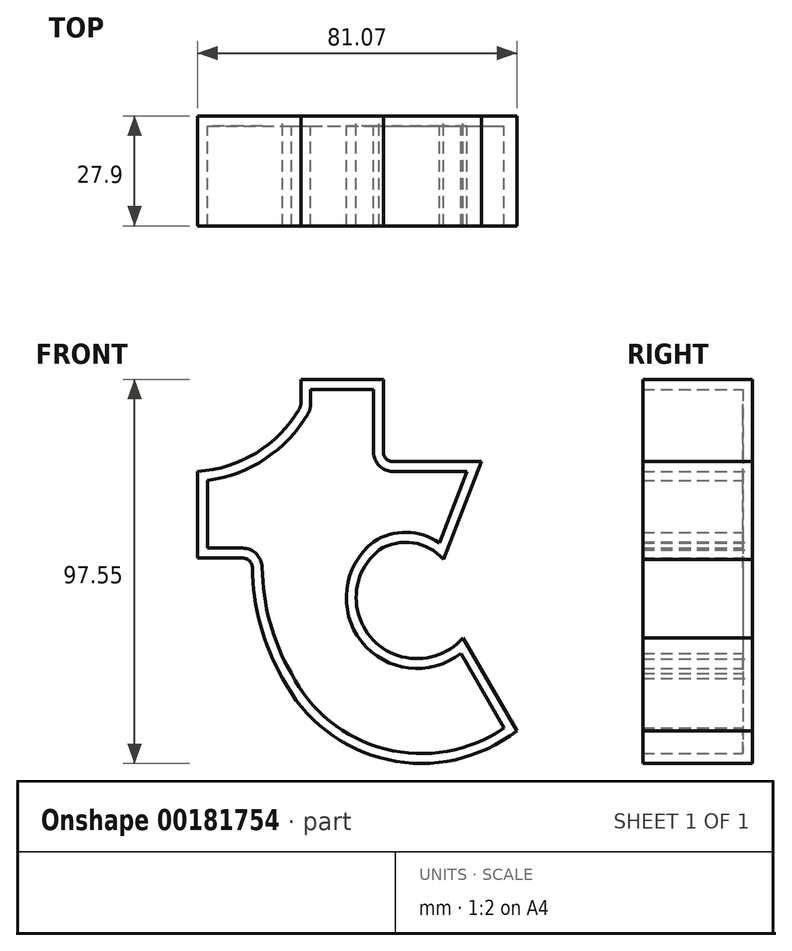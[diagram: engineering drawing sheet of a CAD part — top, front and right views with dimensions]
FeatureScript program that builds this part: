
annotation { "Feature Type Name" : "Feature", "Feature Type Description" : "" }
export const myFeature = defineFeature(function(context is Context, id is Id, definition is map)
    precondition{}
    {
        {
            var Q0;
            Q0=qCreatedBy(makeId("Front.planeOp"),FACE);
            var sketch = newSketch(context, id + "F0", { "sketchPlane" : qUnion([Q0])});
            skText(sketch, "E0", { "text": "t", "fontName": "RobotoSlab-Bold.ttf"});
            const initialGuessF0  = {"E0": [-0.0626, -0.05378, 1, 0, 0.109]};
            skSetInitialGuess(sketch, initialGuessF0);
            skSolve(sketch);
        }
        {
            var Q0;
            Q0=makeQuery(id+"F0.imprint","IMPRINT",FACE,{"disambiguationData":[TD([[makeQuery(id+"F0.imprint","IMPRINT",EDGE,{"derivedFrom":sQuery(id+"F0.wireOp",EDGE,"E0.sketch_text.stroke-0")}),-1.0]])]});
            var sketch = newSketch(context, id + "F1", { "sketchPlane" : qUnion([Q0])});
            skLineSegment(sketch, "E1", {"start": v(-44.06, 46.21) * mm, "end": v(-27.3, 46.21) * mm});
            skLineSegment(sketch, "E2", {"start": v(-27.3, 46.21) * mm, "end": v(-27.3, 29.9) * mm});
            skLineSegment(sketch, "E3", {"start": v(-27.3, 29.9) * mm, "end": v(-3.48, 29.9) * mm});
            skLineSegment(sketch, "E4", {"start": v(-5.08, -16.34) * mm, "end": v(5.84, -35.3) * mm});
            skLineSegment(sketch, "E5", {"start": v(-55.4, 10.4) * mm, "end": v(-69.45, 10.4) * mm});
            skLineSegment(sketch, "E6", {"start": v(-69.45, 10.4) * mm, "end": v(-69.45, 27.63) * mm});
            skArc(sketch, "E7", {"start": v(-27.3, 12) * mm, "mid": v(-30.36, -13.27) * mm, "end": v(-5.08, -16.34) * mm});
            skArc(sketch, "E8", {"start": v(-48.16, -21.43) * mm, "mid": v(-24.3, -40.6) * mm, "end": v(5.84, -35.3) * mm});
            skLineSegment(sketch, "E9", {"start": v(-3.48, 29.9) * mm, "end": v(-10.52, 11.76) * mm});
            skArc(sketch, "E10", {"start": v(-55.4, 10.4) * mm, "mid": v(-54.17, -6.06) * mm, "end": v(-48.16, -21.43) * mm});
            skArc(sketch, "E11", {"start": v(-10.52, 11.76) * mm, "mid": v(-18.87, 14.42) * mm, "end": v(-27.3, 12) * mm});
            skArc(sketch, "E12", {"start": v(-69.45, 27.63) * mm, "mid": v(-53.96, 33.68) * mm, "end": v(-43.02, 46.21) * mm});
            skSolve(sketch);
        }
        {
            var Q0;
            Q0=makeQuery(id+"F1.imprint","IMPRINT",FACE,{"disambiguationData":[TD([[makeQuery(id+"F1.imprint","IMPRINT",EDGE,{"derivedFrom":sQuery(id+"F1.wireOp",EDGE,"E5")}),-1.0]])]});
            var Q1;
            {var subQ24=makeQuery(id+"F0.imprint","IMPRINT",EDGE,{"derivedFrom":sQuery(id+"F0.wireOp",EDGE,"E0.sketch_text.stroke-1")});Q1=makeQuery(id+"F1.imprint","IMPRINT",FACE,{"disambiguationData":[TD([[makeQuery(id+"F1.imprint","IMPRINT",EDGE,{"derivedFrom":subQ24}),-1.0]])]});}
            var Q2;
            {var subQ1=sQuery(id+"F1.wireOp",EDGE,"E9");Q2=makeQuery(id+"F1.imprint","IMPRINT",FACE,{"disambiguationData":[TD([[makeQuery(id+"F1.imprint","IMPRINT",EDGE,{"derivedFrom":subQ1}),-1.0]])]});}
            var Q3;
            {var subQ1=sQuery(id+"F1.wireOp",EDGE,"E4");Q3=makeQuery(id+"F1.imprint","IMPRINT",FACE,{"disambiguationData":[TD([[makeQuery(id+"F1.imprint","IMPRINT",EDGE,{"derivedFrom":subQ1}),-1.0]])]});}
            extrude(context, id + "F2", {"entities" : qUnion([Q0, Q1, Q2, Q3]), "depth" : 25.4 * mm});
        }
        {
            var Q0;
            Q0=makeQuery(id+"F2.opExtrude","SWEPT_FACE",FACE,{"disambiguationData":[OSD([sQuery(id+"F0.wireOp",EDGE,"E0.sketch_text.stroke-19")])]});
            extrude(context, id + "F3", {"entities" : qUnion([Q0]), "operationType" : NewBodyOperationType.ADD, "depth" : 5 * mm});
        }
        {
            var Q0;
            Q0=makeQuery(id+"F2.opExtrude","SWEPT_EDGE",EDGE,{"disambiguationData":[OSD([sQuery(id+"F1.wireOp",EDGE,"E2"),sQuery(id+"F1.wireOp",EDGE,"E3")])]});
            var Q1;
            {var subQ0=sQuery(id+"F1.wireOp",EDGE,"E12");var subQ1=sQuery(id+"F0.wireOp",EDGE,"E0.sketch_text.stroke-19");Q1=makeQuery(id+"F3.boolean.opBoolean","MERGE",EDGE,{"derivedFrom":[makeQuery(id+"F2.opExtrude","SWEPT_EDGE",EDGE,{"disambiguationData":[OSD([subQ1,subQ0])]}),makeQuery(id+"F3.opExtrude","CAP_EDGE",EDGE,{"disambiguationData":[OSD([subQ1,subQ0])],"isStart":true})]});}
            var Q2;
            Q2=makeQuery(id+"F2.opExtrude","SWEPT_EDGE",EDGE,{"disambiguationData":[OSD([sQuery(id+"F1.wireOp",EDGE,"E5"),sQuery(id+"F1.wireOp",EDGE,"E10")])]});
            fillet(context, id + "F4", {"entities" : qUnion([Q0, Q1, Q2]), "radius" : 5 * mm, "tangentPropagation" : true, "allowEdgeOverflow" : false});
        }
        {
            var Q0;
            {var subQ0=sQuery(id+"F0.wireOp",EDGE,"E0.sketch_text.stroke-19");Q0=makeQuery(id+"F3.boolean.opBoolean","MERGE",FACE,{"derivedFrom":[makeQuery(id+"F2.opExtrude","CAP_FACE",FACE,{"disambiguationData":[OSD([subQ0,sQuery(id+"F1.wireOp",EDGE,"E2"),sQuery(id+"F1.wireOp",EDGE,"E3"),sQuery(id+"F1.wireOp",EDGE,"E4"),sQuery(id+"F1.wireOp",EDGE,"E5"),sQuery(id+"F1.wireOp",EDGE,"E6"),sQuery(id+"F1.wireOp",EDGE,"E7"),sQuery(id+"F1.wireOp",EDGE,"E8"),sQuery(id+"F1.wireOp",EDGE,"E9"),sQuery(id+"F1.wireOp",EDGE,"E10"),sQuery(id+"F1.wireOp",EDGE,"E11"),sQuery(id+"F1.wireOp",EDGE,"E12")])],"isStart":false}),makeQuery(id+"F3.opExtrude","SWEPT_FACE",FACE,{"disambiguationData":[OSD([subQ0]),TDD([makeQuery(id+"F2.opExtrude","CAP_EDGE",EDGE,{"disambiguationData":[OSD([subQ0])],"isStart":false})])]})]});}
            shell(context, id + "F5", {"entities" : qUnion([Q0]), "thickness" : 2.5 * mm, "oppositeDirection" : true});
        }
        {
            var Q0;
            Q0=makeQuery(id+"F5.opShell","OFFSET_FACE",FACE,{"disambiguationData":[OSD([sQuery(id+"F0.wireOp",EDGE,"E0.sketch_text.stroke-19"),sQuery(id+"F1.wireOp",EDGE,"E2"),sQuery(id+"F1.wireOp",EDGE,"E3"),sQuery(id+"F1.wireOp",EDGE,"E4"),sQuery(id+"F1.wireOp",EDGE,"E5"),sQuery(id+"F1.wireOp",EDGE,"E6"),sQuery(id+"F1.wireOp",EDGE,"E7"),sQuery(id+"F1.wireOp",EDGE,"E8"),sQuery(id+"F1.wireOp",EDGE,"E9"),sQuery(id+"F1.wireOp",EDGE,"E10"),sQuery(id+"F1.wireOp",EDGE,"E11"),sQuery(id+"F1.wireOp",EDGE,"E12")])]});
            var sketch = newSketch(context, id + "F6", { "sketchPlane" : qUnion([Q0])});
            skLineSegment(sketch, "E13.bottom", {"start": v(14.26, 63.65) * mm, "end": v(-80.74, 63.65) * mm});
            skLineSegment(sketch, "E13.top", {"start": v(14.26, -49.6) * mm, "end": v(-80.74, -49.6) * mm});
            skLineSegment(sketch, "E13.left", {"start": v(14.26, 63.65) * mm, "end": v(14.26, -49.6) * mm});
            skLineSegment(sketch, "E13.right", {"start": v(-80.74, 63.65) * mm, "end": v(-80.74, -49.6) * mm});
            skSolve(sketch);
        }
        {
            var Q0;
            Q0=makeQuery(id+"F6.imprint","IMPRINT",FACE,{"disambiguationData":[TD([[makeQuery(id+"F6.imprint","IMPRINT",EDGE,{"derivedFrom":sQuery(id+"F6.wireOp",EDGE,"E13.bottom")}),1.0]])]});
            extrude(context, id + "F7", {"entities" : qUnion([Q0]), "depth" : 25 * mm});
        }
        {
            var Q0;
            Q0=makeQuery(id+"F7.opExtrude","SWEPT_BODY",BODY,{"disambiguationData":[OSD([sQuery(id+"F0.wireOp",EDGE,"E0.sketch_text.stroke-19"),sQuery(id+"F1.wireOp",EDGE,"E2"),sQuery(id+"F1.wireOp",EDGE,"E3"),sQuery(id+"F1.wireOp",EDGE,"E4"),sQuery(id+"F1.wireOp",EDGE,"E5"),sQuery(id+"F1.wireOp",EDGE,"E6"),sQuery(id+"F1.wireOp",EDGE,"E7"),sQuery(id+"F1.wireOp",EDGE,"E8"),sQuery(id+"F1.wireOp",EDGE,"E9"),sQuery(id+"F1.wireOp",EDGE,"E10"),sQuery(id+"F1.wireOp",EDGE,"E11"),sQuery(id+"F1.wireOp",EDGE,"E12"),sQuery(id+"F6.wireOp",EDGE,"E13.bottom"),sQuery(id+"F6.wireOp",EDGE,"E13.top"),sQuery(id+"F6.wireOp",EDGE,"E13.left"),sQuery(id+"F6.wireOp",EDGE,"E13.right")])]});
            deleteBodies(context, id + "F8", {"entities" : qUnion([Q0])});
        }
    });
